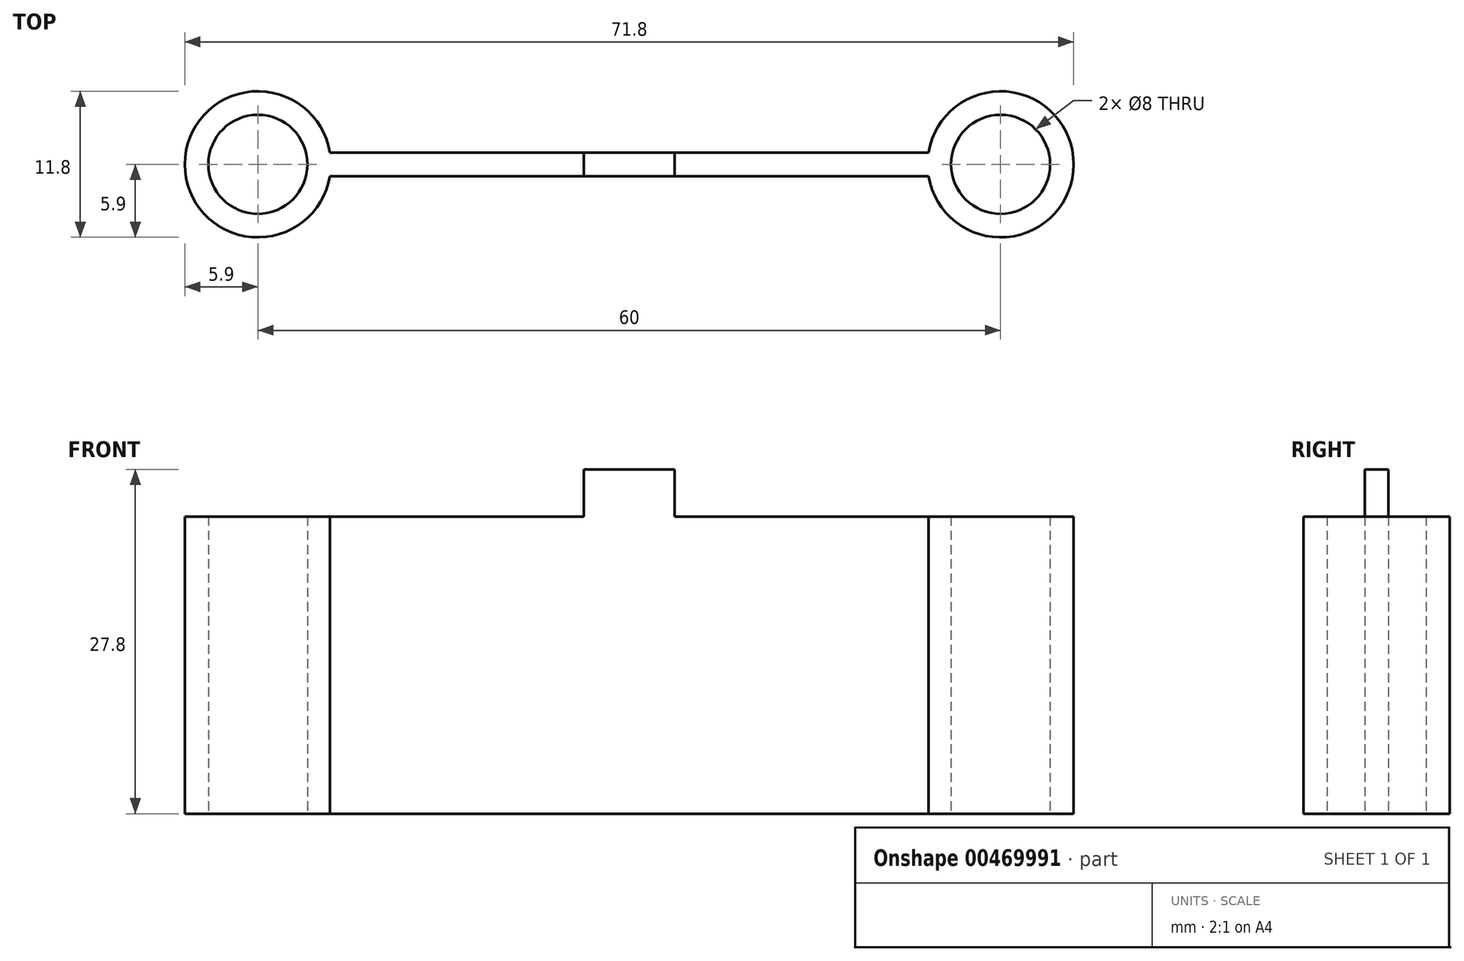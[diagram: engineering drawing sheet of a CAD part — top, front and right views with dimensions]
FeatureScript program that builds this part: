
annotation { "Feature Type Name" : "Feature", "Feature Type Description" : "" }
export const myFeature = defineFeature(function(context is Context, id is Id, definition is map)
    precondition{}
    {
        {
            var Q0;
            Q0=qCreatedBy(makeId("Top.planeOp"),FACE);
            var sketch = newSketch(context, id + "F0", { "sketchPlane" : qUnion([Q0])});
            skLineSegment(sketch, "E0.bottom", {"start": v(-30, 8.54) * mm, "end": v(30, 8.54) * mm, "construction": true});
            skLineSegment(sketch, "E0.top", {"start": v(-30, -8.54) * mm, "end": v(30, -8.54) * mm, "construction": true});
            skLineSegment(sketch, "E0.left", {"start": v(-30, 8.54) * mm, "end": v(-30, -8.54) * mm, "construction": true});
            skLineSegment(sketch, "E0.right", {"start": v(30, 8.54) * mm, "end": v(30, -8.54) * mm, "construction": true});
            skPoint(sketch, "E0.middle", {"position": v(0, 0) * mm});
            skCircle(sketch, "E1", {"center": v(-30, 0) * mm, "radius": 4 * mm});
            skCircle(sketch, "E2", {"center": v(30, 0) * mm, "radius": 4 * mm});
            skLineSegment(sketch, "E3.bottom", {"start": v(-30, 0.95) * mm, "end": v(30, 0.95) * mm});
            skLineSegment(sketch, "E3.top", {"start": v(-30, -0.95) * mm, "end": v(30, -0.95) * mm});
            skLineSegment(sketch, "E3.left", {"start": v(-30, 0.95) * mm, "end": v(-30, -0.95) * mm});
            skLineSegment(sketch, "E3.right", {"start": v(30, 0.95) * mm, "end": v(30, -0.95) * mm});
            skCircle(sketch, "E4.0", {"center": v(-30, 0) * mm, "radius": 5.9 * mm});
            skCircle(sketch, "E5.0", {"center": v(30, 0) * mm, "radius": 5.9 * mm});
            skSolve(sketch);
        }
        {
            var Q0;
            {var subQ0=sQuery(id+"F0.wireOp",EDGE,"E3.bottom");var subQ1=sQuery(id+"F0.wireOp",EDGE,"E1");var subQ2=makeQuery(id+"F0.imprint","INTERSECT",VERTEX,{"derivedFrom":[subQ1,subQ0]});Q0=makeQuery(id+"F0.imprint","IMPRINT",FACE,{"disambiguationData":[TD([[makeQuery(id+"F0.imprint","IMPRINT",EDGE,{"disambiguationData":[TD([[subQ2,1.0]])],"derivedFrom":subQ1}),-1.0]])]});}
            var Q1;
            {var subQ0=sQuery(id+"F0.wireOp",EDGE,"E4.0");var subQ1=sQuery(id+"F0.wireOp",EDGE,"E3.bottom");var subQ2=makeQuery(id+"F0.imprint","INTERSECT",VERTEX,{"derivedFrom":[subQ1,subQ0]});Q1=makeQuery(id+"F0.imprint","IMPRINT",FACE,{"disambiguationData":[TD([[makeQuery(id+"F0.imprint","IMPRINT",EDGE,{"disambiguationData":[TD([[subQ2,-1.0]])],"derivedFrom":subQ1}),-1.0]])]});}
            var Q2;
            {var subQ0=sQuery(id+"F0.wireOp",EDGE,"E3.bottom");var subQ1=sQuery(id+"F0.wireOp",EDGE,"E1");var subQ2=makeQuery(id+"F0.imprint","INTERSECT",VERTEX,{"derivedFrom":[subQ1,subQ0]});Q2=makeQuery(id+"F0.imprint","IMPRINT",FACE,{"disambiguationData":[TD([[makeQuery(id+"F0.imprint","IMPRINT",EDGE,{"disambiguationData":[TD([[subQ2,-1.0]])],"derivedFrom":subQ1}),-1.0]])]});}
            var Q3;
            {var subQ0=sQuery(id+"F0.wireOp",EDGE,"E3.bottom");var subQ1=sQuery(id+"F0.wireOp",EDGE,"E2");var subQ2=makeQuery(id+"F0.imprint","INTERSECT",VERTEX,{"derivedFrom":[subQ1,subQ0]});Q3=makeQuery(id+"F0.imprint","IMPRINT",FACE,{"disambiguationData":[TD([[makeQuery(id+"F0.imprint","IMPRINT",EDGE,{"disambiguationData":[TD([[subQ2,-1.0]])],"derivedFrom":subQ1}),-1.0]])]});}
            var Q4;
            {var subQ0=sQuery(id+"F0.wireOp",EDGE,"E3.bottom");var subQ1=sQuery(id+"F0.wireOp",EDGE,"E2");var subQ2=makeQuery(id+"F0.imprint","INTERSECT",VERTEX,{"derivedFrom":[subQ1,subQ0]});Q4=makeQuery(id+"F0.imprint","IMPRINT",FACE,{"disambiguationData":[TD([[makeQuery(id+"F0.imprint","IMPRINT",EDGE,{"disambiguationData":[TD([[subQ2,1.0]])],"derivedFrom":subQ1}),-1.0]])]});}
            extrude(context, id + "F1", {"entities" : qUnion([Q0, Q1, Q2, Q3, Q4]), "depth" : 24 * mm, "offsetDistance" : 25 * mm});
        }
        {
            var Q0;
            Q0=makeQuery(id+"F1.opExtrude","CAP_FACE",FACE,{"disambiguationData":[OSD([sQuery(id+"F0.wireOp",EDGE,"E1"),sQuery(id+"F0.wireOp",EDGE,"E2"),sQuery(id+"F0.wireOp",EDGE,"E3.bottom"),sQuery(id+"F0.wireOp",EDGE,"E3.top"),sQuery(id+"F0.wireOp",EDGE,"E4.0"),sQuery(id+"F0.wireOp",EDGE,"E5.0")])],"isStart":false});
            var sketch = newSketch(context, id + "F2", { "sketchPlane" : qUnion([Q0])});
            skLineSegment(sketch, "E6.bottom", {"start": v(-3.65, 0.95) * mm, "end": v(3.65, 0.95) * mm});
            skLineSegment(sketch, "E6.top", {"start": v(-3.65, -0.95) * mm, "end": v(3.65, -0.95) * mm});
            skLineSegment(sketch, "E6.left", {"start": v(-3.65, 0.95) * mm, "end": v(-3.65, -0.95) * mm});
            skLineSegment(sketch, "E6.right", {"start": v(3.65, 0.95) * mm, "end": v(3.65, -0.95) * mm});
            skPoint(sketch, "E6.middle", {"position": v(0, 0) * mm});
            skSolve(sketch);
        }
        {
            var Q0;
            Q0=makeQuery(id+"F2.imprint","IMPRINT",FACE,{"disambiguationData":[TD([[makeQuery(id+"F2.imprint","IMPRINT",EDGE,{"derivedFrom":sQuery(id+"F2.wireOp",EDGE,"E6.bottom")}),-1.0]])]});
            extrude(context, id + "F3", {"entities" : qUnion([Q0]), "operationType" : NewBodyOperationType.ADD, "depth" : 3.8 * mm, "offsetDistance" : 25 * mm});
        }
    });
